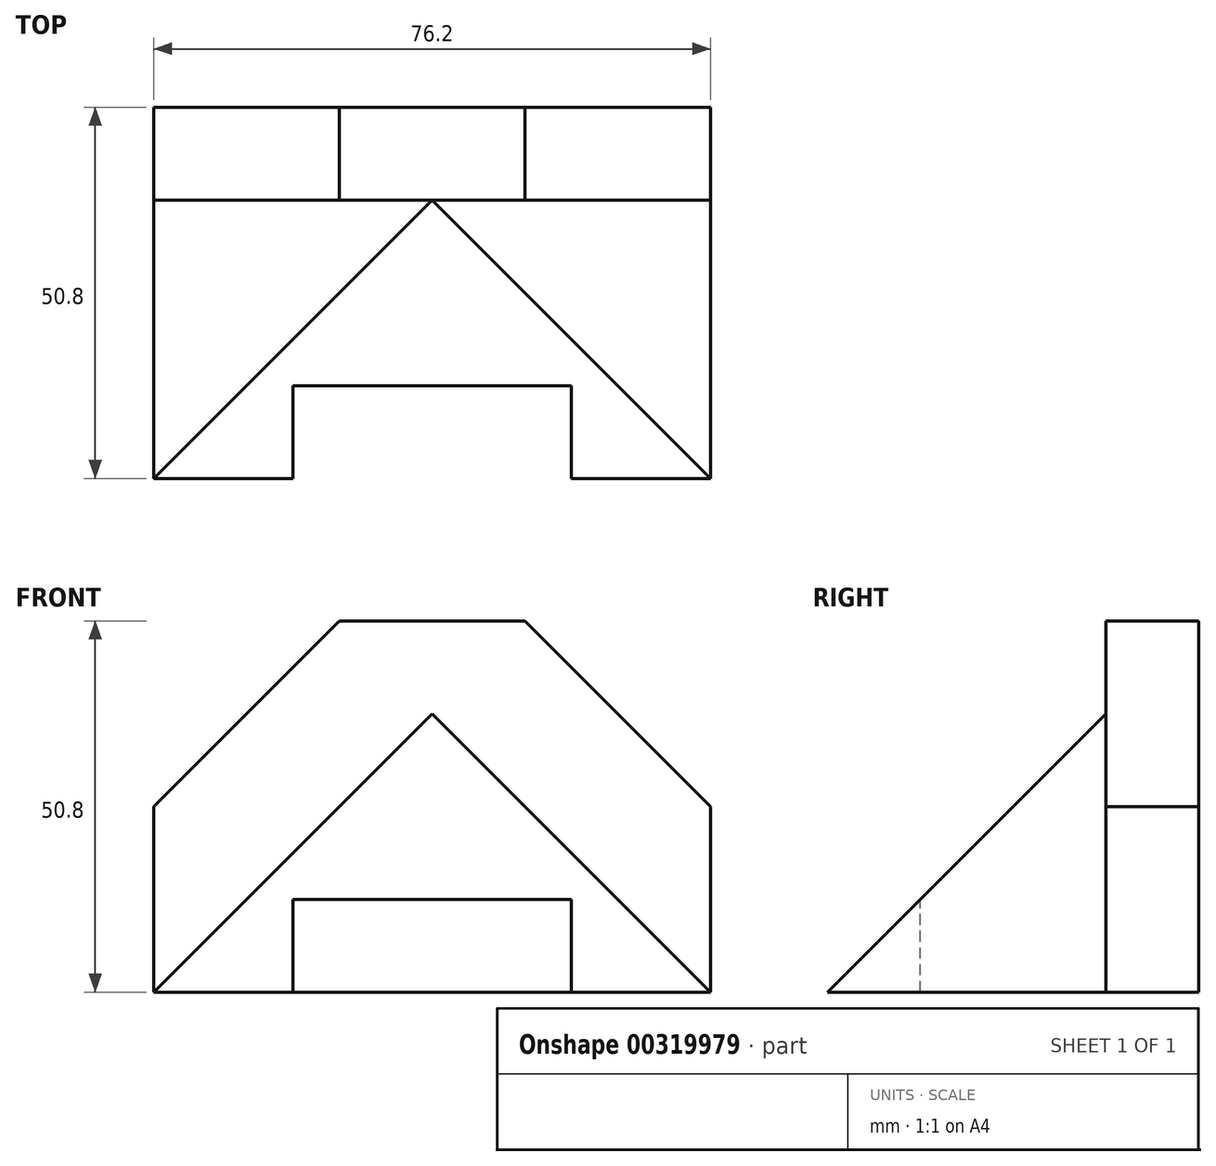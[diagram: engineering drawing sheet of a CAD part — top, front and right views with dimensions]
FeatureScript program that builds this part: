
annotation { "Feature Type Name" : "Feature", "Feature Type Description" : "" }
export const myFeature = defineFeature(function(context is Context, id is Id, definition is map)
    precondition{}
    {
        {
            var Q0;
            Q0=qCreatedBy(makeId("Front.planeOp"),FACE);
            var sketch = newSketch(context, id + "F0", { "sketchPlane" : qUnion([Q0])});
            skLineSegment(sketch, "E0.bottom", {"start": v(0, 0) * mm, "end": v(76.2, 0) * mm});
            skLineSegment(sketch, "E0.top", {"start": v(0, 50.8) * mm, "end": v(76.2, 50.8) * mm});
            skLineSegment(sketch, "E0.left", {"start": v(0, 0) * mm, "end": v(0, 50.8) * mm});
            skLineSegment(sketch, "E0.right", {"start": v(76.2, 0) * mm, "end": v(76.2, 50.8) * mm});
            skSolve(sketch);
        }
        {
            var Q0;
            Q0 = qSketchRegion(id + "F0", true);
            extrude(context, id + "F1", {"entities" : qUnion([Q0]), "oppositeDirection" : true, "depth" : 50.8 * mm});
        }
        {
            var Q0;
            Q0=makeQuery(id+"F1.opExtrude","SWEPT_FACE",FACE,{"disambiguationData":[OSD([sQuery(id+"F0.wireOp",EDGE,"E0.top")])]});
            var sketch = newSketch(context, id + "F2", { "sketchPlane" : qUnion([Q0])});
            skLineSegment(sketch, "E1.bottom", {"start": v(19.05, 0) * mm, "end": v(57.15, 0) * mm});
            skLineSegment(sketch, "E1.top", {"start": v(19.05, 12.7) * mm, "end": v(57.15, 12.7) * mm});
            skLineSegment(sketch, "E1.left", {"start": v(19.05, 0) * mm, "end": v(19.05, 12.7) * mm});
            skLineSegment(sketch, "E1.right", {"start": v(57.15, 0) * mm, "end": v(57.15, 12.7) * mm});
            skSolve(sketch);
        }
        {
            var Q0;
            Q0=makeQuery(id+"F2.imprint","IMPRINT",FACE,{"disambiguationData":[TD([[makeQuery(id+"F2.imprint","IMPRINT",EDGE,{"derivedFrom":sQuery(id+"F2.wireOp",EDGE,"E1.bottom")}),1.0]])]});
            extrude(context, id + "F3", {"entities" : qUnion([Q0]), "operationType" : NewBodyOperationType.REMOVE, "endBound" : BoundingType.THROUGH_ALL, "oppositeDirection" : true, "depth" : 25.4 * mm});
        }
        {
            var Q0;
            Q0=makeQuery(id+"F1.opExtrude","CAP_FACE",FACE,{"disambiguationData":[OSD([sQuery(id+"F0.wireOp",EDGE,"E0.bottom"),sQuery(id+"F0.wireOp",EDGE,"E0.top"),sQuery(id+"F0.wireOp",EDGE,"E0.left"),sQuery(id+"F0.wireOp",EDGE,"E0.right")])],"isStart":false});
            var sketch = newSketch(context, id + "F4", { "sketchPlane" : qUnion([Q0])});
            skLineSegment(sketch, "E2", {"start": v(-76.2, 50.8) * mm, "end": v(-76.2, 25.4) * mm});
            skLineSegment(sketch, "E3", {"start": v(-76.2, 50.8) * mm, "end": v(-50.8, 50.8) * mm});
            skLineSegment(sketch, "E4", {"start": v(-50.8, 50.8) * mm, "end": v(-76.2, 25.4) * mm});
            skLineSegment(sketch, "E5", {"start": v(0, 50.8) * mm, "end": v(-25.4, 50.8) * mm});
            skLineSegment(sketch, "E6", {"start": v(-25.4, 50.8) * mm, "end": v(0, 25.4) * mm});
            skLineSegment(sketch, "E7", {"start": v(0, 25.4) * mm, "end": v(0, 50.8) * mm});
            skSolve(sketch);
        }
        {
            var Q0;
            Q0 = qSketchRegion(id + "F4", true);
            extrude(context, id + "F5", {"entities" : qUnion([Q0]), "operationType" : NewBodyOperationType.REMOVE, "oppositeDirection" : true, "depth" : 12.7 * mm});
        }
        {
            var Q0;
            Q0=makeQuery(id+"F1.opExtrude","SWEPT_FACE",FACE,{"disambiguationData":[OSD([sQuery(id+"F0.wireOp",EDGE,"E0.right")])]});
            var sketch = newSketch(context, id + "F6", { "sketchPlane" : qUnion([Q0])});
            skLineSegment(sketch, "E8", {"start": v(0, 0) * mm, "end": v(0, 38.1) * mm});
            skLineSegment(sketch, "E9", {"start": v(0, 0) * mm, "end": v(38.1, 38.1) * mm});
            skLineSegment(sketch, "E10", {"start": v(38.1, 38.1) * mm, "end": v(0, 38.1) * mm});
            skLineSegment(sketch, "E11", {"start": v(0, 38.1) * mm, "end": v(0, 50.8) * mm});
            skLineSegment(sketch, "E12", {"start": v(0, 50.8) * mm, "end": v(38.1, 50.8) * mm});
            skLineSegment(sketch, "E13", {"start": v(38.1, 50.8) * mm, "end": v(38.1, 38.1) * mm});
            skSolve(sketch);
        }
        {
            var Q0;
            Q0=makeQuery(id+"F6.imprint","IMPRINT",FACE,{"disambiguationData":[TD([[makeQuery(id+"F6.imprint","IMPRINT",EDGE,{"derivedFrom":sQuery(id+"F6.wireOp",EDGE,"E10")}),-1.0]])]});
            extrude(context, id + "F7", {"entities" : qUnion([Q0]), "operationType" : NewBodyOperationType.REMOVE, "endBound" : BoundingType.THROUGH_ALL, "oppositeDirection" : true, "depth" : 25.4 * mm});
        }
        {
            var Q0;
            Q0=makeQuery(id+"F6.imprint","IMPRINT",FACE,{"disambiguationData":[TD([[makeQuery(id+"F6.imprint","IMPRINT",EDGE,{"derivedFrom":sQuery(id+"F6.wireOp",EDGE,"E8")}),-1.0]])]});
            var Q1;
            Q1=makeQuery(id+"F6.imprint","IMPRINT",FACE,{"disambiguationData":[TD([[makeQuery(id+"F6.imprint","IMPRINT",EDGE,{"derivedFrom":sQuery(id+"F6.wireOp",EDGE,"E10")}),-1.0]])]});
            extrude(context, id + "F8", {"entities" : qUnion([Q0, Q1]), "operationType" : NewBodyOperationType.REMOVE, "endBound" : BoundingType.THROUGH_ALL, "oppositeDirection" : true, "depth" : 25.4 * mm});
        }
        {
            var Q0;
            Q0=makeQuery(id+"F7.boolean.opBoolean","COPY",FACE,{"derivedFrom":makeQuery(id+"F7.opExtrude","SWEPT_FACE",FACE,{"disambiguationData":[OSD([sQuery(id+"F6.wireOp",EDGE,"E13")])]})});
            var sketch = newSketch(context, id + "F9", { "sketchPlane" : qUnion([Q0])});
            skLineSegment(sketch, "E14", {"start": v(38.1, 38.1) * mm, "end": v(0, 0) * mm});
            skLineSegment(sketch, "E15", {"start": v(0, 0) * mm, "end": v(0, 38.1) * mm});
            skLineSegment(sketch, "E16", {"start": v(0, 38.1) * mm, "end": v(38.1, 38.1) * mm});
            skLineSegment(sketch, "E17", {"start": v(38.1, 38.1) * mm, "end": v(76.2, 0) * mm});
            skLineSegment(sketch, "E18", {"start": v(76.2, 0) * mm, "end": v(76.2, 38.1) * mm});
            skLineSegment(sketch, "E19", {"start": v(76.2, 38.1) * mm, "end": v(38.1, 38.1) * mm});
            skSolve(sketch);
        }
        {
            var Q0;
            Q0 = qSketchRegion(id + "F9", true);
            extrude(context, id + "F10", {"entities" : qUnion([Q0]), "operationType" : NewBodyOperationType.REMOVE, "endBound" : BoundingType.THROUGH_ALL, "depth" : 25.4 * mm});
        }
    });
